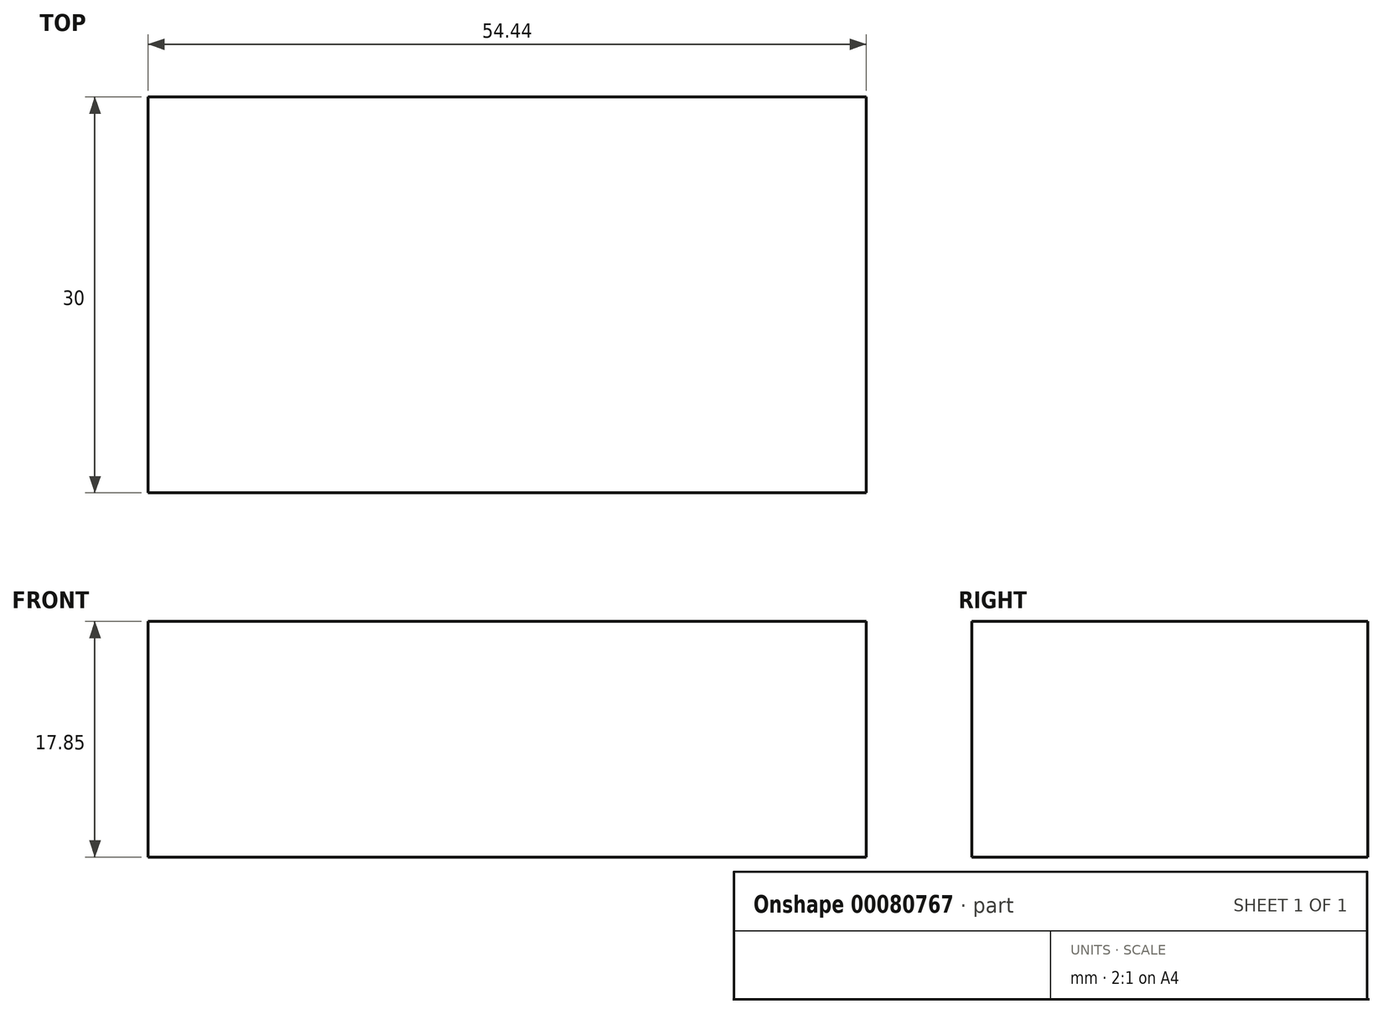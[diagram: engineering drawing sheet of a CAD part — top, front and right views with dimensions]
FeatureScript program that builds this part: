
annotation { "Feature Type Name" : "Feature", "Feature Type Description" : "" }
export const myFeature = defineFeature(function(context is Context, id is Id, definition is map)
    precondition{}
    {
        {
            var Q0;
            Q0=qCreatedBy(makeId("Top.planeOp"),FACE);
            var sketch = newSketch(context, id + "F0", { "sketchPlane" : qUnion([Q0])});
            skLineSegment(sketch, "E0.bottom", {"start": v(27.22, 15) * mm, "end": v(-27.22, 15) * mm});
            skLineSegment(sketch, "E0.top", {"start": v(27.22, -15) * mm, "end": v(-27.22, -15) * mm});
            skLineSegment(sketch, "E0.left", {"start": v(27.22, 15) * mm, "end": v(27.22, -15) * mm});
            skLineSegment(sketch, "E0.right", {"start": v(-27.22, 15) * mm, "end": v(-27.22, -15) * mm});
            skPoint(sketch, "E0.middle", {"position": v(0, 0) * mm});
            skSolve(sketch);
        }
        {
            var Q0;
            Q0 = qSketchRegion(id + "F0", true);
            extrude(context, id + "F1", {"entities" : qUnion([Q0]), "depth" : 17.85 * mm});
        }
    });
